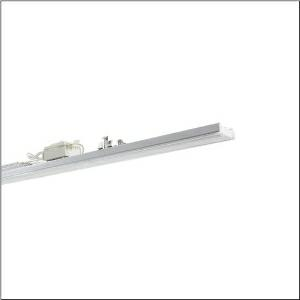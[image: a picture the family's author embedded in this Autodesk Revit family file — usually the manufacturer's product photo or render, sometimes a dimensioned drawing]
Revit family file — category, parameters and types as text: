
# Revit family: licross_r__21_recessed_ho_52tl11dn4axs_508c
name_source: partatom
category: Lighting Fixtures
units: mm (PartAtom-declared; Revit-internal decimal feet)

## family parameters
Cut with Voids When Loaded = No
Host = Face
Light Source = No
Part Type = Normal
Room Calculation Point = No
Round Connector Dimension = Use Diameter
Shared = No

## types (1)
- --- (1 x LED, 10000 lm, 54.7 W, 4000K)
    Apparent Load = 55 VA
    CIE Flux Codes = 87 95 99 100 100
    Color Rendering = 80
    Color Temperature = 4000K
    Default Elevation = 1800 mm
    Description = Licross® 21 Recessed HO, luminaire insert, of sheet steel, galvanised, coil coated, white, length: 1.500mm, width: 66mm, height: 67mm, LED rated luminous flux: 10.000lm, light colour: 840, control gear: DALI 2, with plug, 5-pole, with phase selection, mains connection: 220..240V, AC, 50/60Hz, rated input power: 55W, halogen-free wiring, primary light control with lens, of plastic, primary optical cover: cover, of PMMA, light emission: direct distribution, primary light characteristic: symmetric, protection rating (complete): IP40, insulation class (complete): insulation class I (protective earthing), certification: CE, ENEC, VDE, UKCA, protection symbol: D if used in an environment without relevant dust loads with corresponding accessories, impact resistance: IK06, permissible ambient temperature for indoor applications: -25..+40°C, corresponds to IFS (International Featured Standards) requirements for safety and quality in the food industry, reducing of maximum allowable ambient temperature of 5°C with ceiling mounting, LABS conformity tested according to VDMA 24364:2018-05, packaging unit: 1 piece
    Height = 58 mm
    Lamp = 1 x LED
    Lamp Light Flux = 10000 lm
    Lamp Power = 54.7 W
    Lamp count = 1
    Length = 1500 mm
    Luminous efficacy = 183 lm/W
    Manufacturer = Siteco
    ModVariant = No
    Model = 52TL11DN4AXS
    Mounting Place = Ceiling
    Mounting Type = Pendant
    Number of Poles = 1
    OnlyDefault = Yes
    Power Factor = 1
    Product Name = Licross® 21 Recessed HO
    Product group = luminaire insert
    ProductGroupID = 902
    Protection Class = Protection class I
    Protection Degree = IP 40
    RLX_Detail_Level = 1
    RLX_Emergency_Light_Flux = 0 lm
    RLX_Emergency_Type = 0
    RLX_Emergency_Type_DB = No
    RlxData = <blob elided: 24381 chars, md5=c18d4498>
    Socket = socket
    Standby Power = 0 W
    System Light Flux = 10000 lm
    System Power = 55 W
    Type Comments = factory setting: luminous flux: 100 % | dim-lin: 254 | 313 mA
    Type Image = l_1296930.jpg
    URL = http://relux.com
    VarID = @adj_127254
    Voltage = 0 V
    Weight = 0.00 kg
    Width = 66 mm

## geometry (parser evidence)
native form markers: Blend x4, Sweep x10
no freeform markers — native parametric forms only
